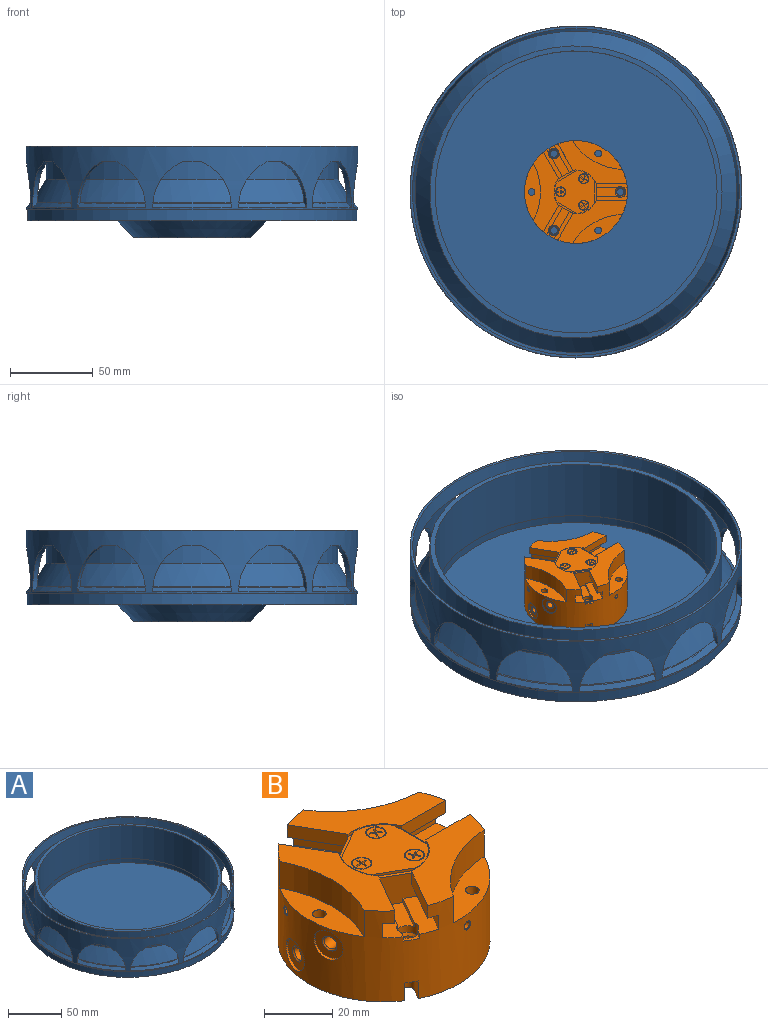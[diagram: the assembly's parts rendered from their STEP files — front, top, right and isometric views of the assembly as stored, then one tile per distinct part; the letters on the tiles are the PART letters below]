
ASSEMBLY  parts=2 mates=1
PART A: 64 faces, bbox 200x200x54.8 mm
  f0: cylinder r=100mm len=200mm, axis (0,0,1), area 11248.3mm2, adj f3,f4,f9,f10,f11,f12,f13,f14
  f1: plane 176x176mm, normal (0,0,1), area 1630.5mm2, adj f2,f5
  f2: cylinder r=85mm len=170mm, axis (0,0,1), area 20209.2mm2, adj f1,f61
  f3: plane 200x200mm, normal (0,0,-1), area 398.3mm2, adj f0,f58
  f4: plane 200x200mm, normal (0,0,1), area 935.4mm2, adj f0,f7
  f5: cylinder r=88mm len=176mm, axis (0,0,1), area 10969.9mm2, adj f1,f8
  f6: cylinder r=97mm len=194mm, axis (0,0,1), area 4810mm2, adj f7,f8,f9,f10,f11,f12,f13,f14
  f7: cone r=97mm half-angle=9.5deg, axis (0,0,1), area 5603.9mm2, adj f4,f6
  f8: cone r=88mm half-angle=31.3deg, axis (0,0,-1), area 10065.3mm2, adj f5,f6
  f9: plane 10.97x3.16mm, normal (0,0,-1), area 32.9mm2, adj f0,f6,f10,f11
  f10: cylinder r=28.77mm len=27.57mm, axis (0,-1,0), area 102.7mm2, adj f0,f6,f9,f12
  f11: cylinder r=28.77mm len=27.57mm, axis (0,-1,0), area 102.7mm2, adj f0,f6,f9,f12
  f12: cone r=100mm half-angle=45deg, axis (0,0,-1), area 202.5mm2, adj f0,f6,f10,f11
  f13: plane 11x8.09mm, normal (0,0,-1), area 32.9mm2, adj f0,f6,f14,f15
  f14: cylinder r=28.77mm len=27.57mm, axis (0.5,-0.87,0), area 102.7mm2, adj f0,f6,f13,f16
  f15: cylinder r=28.77mm len=27.57mm, axis (0.5,-0.87,0), area 102.7mm2, adj f0,f6,f13,f16
  f16: cone r=100mm half-angle=45deg, axis (0,0,-1), area 202.5mm2, adj f0,f6,f14,f15
  f17: cylinder r=28.77mm len=27.57mm, axis (0.87,-0.5,0), area 102.7mm2, adj f0,f6,f18,f20
  f18: plane 11x8.09mm, normal (0,0,-1), area 32.9mm2, adj f0,f6,f17,f19
  f19: cylinder r=28.77mm len=27.57mm, axis (0.87,-0.5,0), area 102.7mm2, adj f0,f6,f18,f20
  f20: cone r=100mm half-angle=45deg, axis (0,0,-1), area 202.5mm2, adj f0,f6,f17,f19
  f21: cylinder r=28.77mm len=27.57mm, axis (1,0,0), area 102.7mm2, adj f0,f6,f22,f24
  f22: plane 10.97x3.16mm, normal (0,0,-1), area 32.9mm2, adj f0,f6,f21,f23
  f23: cylinder r=28.77mm len=27.57mm, axis (1,0,0), area 102.7mm2, adj f0,f6,f22,f24
  f24: cone r=100mm half-angle=45deg, axis (0,0,-1), area 202.5mm2, adj f0,f6,f21,f23
  f25: cylinder r=28.77mm len=27.57mm, axis (0.87,0.5,0), area 102.7mm2, adj f0,f6,f26,f28
  f26: plane 11x8.09mm, normal (0,0,-1), area 32.9mm2, adj f0,f6,f25,f27
  f27: cylinder r=28.77mm len=27.57mm, axis (0.87,0.5,0), area 102.7mm2, adj f0,f6,f26,f28
  f28: cone r=100mm half-angle=45deg, axis (0,0,-1), area 202.5mm2, adj f0,f6,f25,f27
  f29: cylinder r=28.77mm len=27.57mm, axis (0.5,0.87,0), area 102.7mm2, adj f0,f6,f30,f32
  f30: plane 11x8.09mm, normal (0,0,-1), area 32.9mm2, adj f0,f6,f29,f31
  f31: cylinder r=28.77mm len=27.57mm, axis (0.5,0.87,0), area 102.7mm2, adj f0,f6,f30,f32
  f32: cone r=100mm half-angle=45deg, axis (0,0,-1), area 202.5mm2, adj f0,f6,f29,f31
  f33: cylinder r=28.77mm len=27.57mm, axis (0,1,0), area 102.7mm2, adj f0,f6,f34,f36
  f34: plane 10.97x3.16mm, normal (0,0,-1), area 32.9mm2, adj f0,f6,f33,f35
  f35: cylinder r=28.77mm len=27.57mm, axis (0,1,0), area 102.7mm2, adj f0,f6,f34,f36
  f36: cone r=100mm half-angle=45deg, axis (0,0,-1), area 202.5mm2, adj f0,f6,f33,f35
  f37: cylinder r=28.77mm len=27.57mm, axis (-0.5,0.87,0), area 102.7mm2, adj f0,f6,f38,f40
  f38: plane 11x8.09mm, normal (0,0,-1), area 32.9mm2, adj f0,f6,f37,f39
  f39: cylinder r=28.77mm len=27.57mm, axis (-0.5,0.87,0), area 102.7mm2, adj f0,f6,f38,f40
  f40: cone r=100mm half-angle=45deg, axis (0,0,-1), area 202.5mm2, adj f0,f6,f37,f39
  f41: plane 11x8.09mm, normal (0,0,-1), area 32.9mm2, adj f0,f6,f42,f43
  f42: cylinder r=28.77mm len=27.57mm, axis (-0.87,0.5,0), area 102.7mm2, adj f0,f6,f41,f44
  f43: cylinder r=28.77mm len=27.57mm, axis (-0.87,0.5,0), area 102.7mm2, adj f0,f6,f41,f44
  f44: cone r=100mm half-angle=45deg, axis (0,0,-1), area 202.5mm2, adj f0,f6,f42,f43
  f45: plane 10.97x3.16mm, normal (0,0,-1), area 32.9mm2, adj f0,f6,f46,f47
  f46: cylinder r=28.77mm len=27.57mm, axis (-1,0,0), area 102.7mm2, adj f0,f6,f45,f48
  f47: cylinder r=28.77mm len=27.57mm, axis (-1,0,0), area 102.7mm2, adj f0,f6,f45,f48
  f48: cone r=100mm half-angle=45deg, axis (0,0,-1), area 202.5mm2, adj f0,f6,f46,f47
  f49: plane 11x8.09mm, normal (0,0,-1), area 32.9mm2, adj f0,f6,f50,f51
  f50: cylinder r=28.77mm len=27.57mm, axis (-0.87,-0.5,0), area 102.7mm2, adj f0,f6,f49,f52
  f51: cylinder r=28.77mm len=27.57mm, axis (-0.87,-0.5,0), area 102.7mm2, adj f0,f6,f49,f52
  f52: cone r=100mm half-angle=45deg, axis (0,0,-1), area 202.5mm2, adj f0,f6,f50,f51
  f53: plane 11x8.09mm, normal (0,0,-1), area 32.9mm2, adj f0,f6,f54,f55
  f54: cylinder r=28.77mm len=27.57mm, axis (-0.5,-0.87,0), area 102.7mm2, adj f0,f6,f53,f56
  f55: cylinder r=28.77mm len=27.57mm, axis (-0.5,-0.87,0), area 102.7mm2, adj f0,f6,f53,f56
  f56: cone r=100mm half-angle=45deg, axis (0,0,-1), area 202.5mm2, adj f0,f6,f54,f55
  f57: plane 198.73x198.73mm, normal (0,0,-1), area 24655.9mm2, adj f58,f63
  f58: cylinder r=99.36mm len=198.73mm, axis (0,0,1), area 4370.3mm2, adj f3,f57
  f59: cylinder r=85.05mm len=170.1mm, axis (0,0,1), area 2671.9mm2, adj f60,f61
  f60: plane 170.1x170.1mm, normal (0,0,1), area 22725.1mm2, adj f59
  f61: plane 170.1x170.1mm, normal (0,0,-1), area 27.1mm2, adj f2,f59
  f62: plane 70x70mm, normal (0,0,-1), area 3848.5mm2, adj f63
  f63: cone r=35mm half-angle=45deg, axis (0,0,1), area 3554.3mm2, adj f57,f62
PART B: 183 faces, bbox 62.3x62x32.5 mm
  f0: plane 4.13x4.03mm, normal (-0.97,-0.22,0), area 10.9mm2, adj f1,f2,f163,f165
  f1: cylinder r=2.07mm len=5.38mm, axis (-0.97,-0.22,0), area 53.1mm2, adj f0,f2,f43,f164,f165
  f2: cylinder r=2.07mm len=0.55mm, axis (-0.97,-0.22,0), area 0mm2, adj f0,f1,f165
  f3: plane 4.13x4.03mm, normal (-0.97,0.22,0), area 11.7mm2, adj f4,f159,f161
  f4: cylinder r=2.07mm len=5.38mm, axis (-0.97,0.22,0), area 54mm2, adj f3,f40,f160,f161
  f5: cylinder r=31mm len=62mm, axis (0,0,-1), area 4600.2mm2, adj f9,f10,f11,f12,f13,f14,f18,f19
  f6: cylinder r=2.18mm len=7.57mm, axis (0,0,-1), area 68.3mm2, adj f9,f10,f81,f90,f158
  f7: cylinder r=2.18mm len=7.57mm, axis (0,0,-1), area 68.3mm2, adj f11,f12,f85,f91,f158
  f8: cylinder r=2.18mm len=7.57mm, axis (0,0,-1), area 68.3mm2, adj f13,f14,f89,f92,f158
  f9: plane 6.32x3.09mm, normal (0.87,-0.5,0), area 22.6mm2, adj f5,f6,f90,f158
  f10: plane 6.32x3.09mm, normal (-0.87,0.5,0), area 22.6mm2, adj f5,f6,f90,f158
  f11: plane 6.32x3.09mm, normal (0.87,0.5,0), area 22.6mm2, adj f5,f7,f91,f158
  f12: plane 6.32x3.09mm, normal (-0.87,-0.5,0), area 22.6mm2, adj f5,f7,f91,f158
  f13: plane 6.32x3.57mm, normal (0,-1,0), area 22.6mm2, adj f5,f8,f92,f158
  f14: plane 6.32x3.57mm, normal (0,1,0), area 22.6mm2, adj f5,f8,f92,f158
  f15: cone r=0mm half-angle=45deg, axis (0,0,1), area 6.3mm2, adj f112,f143
  f16: cone r=0mm half-angle=45deg, axis (0,0,1), area 6.3mm2, adj f112,f128
  f17: cone r=0mm half-angle=45deg, axis (0,0,1), area 6.3mm2, adj f112,f113
  f18: plane 41.56x25.92mm, normal (0,0,1), area 418mm2, adj f5,f52,f62,f75,f102
  f19: plane 47.99x15.19mm, normal (0,0,1), area 418mm2, adj f5,f53,f70,f73,f104
  f20: plane 14.77x10.14mm, normal (-0.5,0.87,0), area 129.5mm2, adj f29,f30,f31,f45,f46,f47,f49,f50
  f21: plane 17.05x10.14mm, normal (1,0,0), area 129.5mm2, adj f24,f25,f26,f54,f55,f56,f58,f59
  f22: plane 14.77x10.14mm, normal (-0.5,-0.87,0), area 129.5mm2, adj f34,f36,f63,f64,f65,f66,f67,f68
  f23: plane 2.19x1.5mm, normal (0,1,0), area 3.3mm2, adj f5,f56,f57,f86
  f24: plane 12.67x1.5mm, normal (0,1,0), area 19mm2, adj f21,f25,f56,f86
  f25: plane 12.67x5mm, normal (0,0,1), area 59.1mm2, adj f21,f24,f26,f86
  f26: plane 12.67x1.5mm, normal (0,-1,0), area 19mm2, adj f21,f25,f58,f86
  f27: plane 2.19x1.5mm, normal (0,-1,0), area 3.3mm2, adj f5,f57,f58,f86
  f28: plane 1.89x1.5mm, normal (-0.87,-0.5,0), area 3.3mm2, adj f5,f47,f48,f82
  f29: plane 10.97x6.33mm, normal (-0.87,-0.5,0), area 19mm2, adj f20,f30,f47,f82
  f30: plane 13.47x10.66mm, normal (0,0,1), area 59.1mm2, adj f20,f29,f31,f82
  f31: plane 10.97x6.33mm, normal (0.87,0.5,0), area 19mm2, adj f20,f30,f49,f82
  f32: plane 1.89x1.5mm, normal (0.87,0.5,0), area 3.3mm2, adj f5,f48,f49,f82
  f33: plane 1.89x1.5mm, normal (0.87,-0.5,0), area 3.3mm2, adj f5,f35,f65,f78
  f34: plane 10.97x6.33mm, normal (0.87,-0.5,0), area 19mm2, adj f22,f65,f66,f78
  f35: plane 5.42x4.39mm, normal (0,0,1), area 7mm2, adj f5,f33,f37,f78
  f36: plane 10.97x6.33mm, normal (-0.87,0.5,0), area 19mm2, adj f22,f66,f67,f78
  f37: plane 1.89x1.5mm, normal (-0.87,0.5,0), area 3.3mm2, adj f5,f35,f67,f78
  f38: plane 41.56x25.92mm, normal (0,0,1), area 418mm2, adj f5,f61,f71,f77,f103
  f39: cylinder r=5mm len=10mm, axis (-0.97,0.22,0), area 25.1mm2, adj f5,f41
  f40: cone r=2.07mm half-angle=45deg, axis (-0.97,0.22,0), area 8.8mm2, adj f4,f41
  f41: plane 10x9.74mm, normal (-0.97,0.22,0), area 58.9mm2, adj f39,f40
  f42: cylinder r=5mm len=10mm, axis (-0.97,-0.22,0), area 25.1mm2, adj f5,f44
  f43: cone r=2.07mm half-angle=45deg, axis (-0.97,-0.22,0), area 8.8mm2, adj f1,f44
  f44: plane 10x9.74mm, normal (-0.97,-0.22,0), area 58.9mm2, adj f42,f43
  f45: plane 17.09x12.3mm, normal (0,0,-1), area 63.9mm2, adj f5,f20,f46,f52
  f46: plane 15.33x8.85mm, normal (-0.87,-0.5,0), area 89.4mm2, adj f5,f20,f45,f47
  f47: plane 18.34x14.62mm, normal (0,0,1), area 108.7mm2, adj f5,f20,f28,f29,f46,f82
  f48: plane 5.42x4.39mm, normal (0,0,1), area 7mm2, adj f5,f28,f32,f82
  f49: plane 19.29x14.07mm, normal (0,0,1), area 108.7mm2, adj f5,f20,f31,f32,f50,f82
  f50: plane 15.33x8.85mm, normal (0.87,0.5,0), area 89.4mm2, adj f5,f20,f49,f51
  f51: plane 17.78x11.9mm, normal (0,0,-1), area 63.9mm2, adj f5,f20,f50,f53
  f52: plane 16.01x9.25mm, normal (-0.87,-0.5,0), area 83.1mm2, adj f5,f18,f20,f45,f102,f105
  f53: plane 16.01x9.25mm, normal (0.87,0.5,0), area 83.1mm2, adj f5,f19,f20,f51,f104,f105
  f54: plane 18.49x3.53mm, normal (0,0,-1), area 63.9mm2, adj f5,f21,f55,f61
  f55: plane 17.7x5.05mm, normal (0,1,0), area 89.4mm2, adj f5,f21,f54,f56
  f56: plane 18.8x6.03mm, normal (0,0,1), area 108.7mm2, adj f5,f21,f23,f24,f55,f86
  f57: plane 5x2.29mm, normal (0,0,1), area 7mm2, adj f5,f23,f27,f86
  f58: plane 18.8x6.03mm, normal (0,0,1), area 108.7mm2, adj f5,f21,f26,f27,f59,f86
  f59: plane 17.7x5.05mm, normal (0,-1,0), area 89.4mm2, adj f5,f21,f58,f60
  f60: plane 18.49x3.53mm, normal (0,0,-1), area 63.9mm2, adj f5,f21,f59,f62
  f61: plane 18.49x4.5mm, normal (0,1,0), area 83.1mm2, adj f5,f21,f38,f54,f103,f105
  f62: plane 18.49x4.5mm, normal (0,-1,0), area 83.1mm2, adj f5,f18,f21,f60,f102,f105
  f63: plane 17.78x11.9mm, normal (0,0,-1), area 63.9mm2, adj f5,f22,f64,f70
  f64: plane 15.33x8.85mm, normal (0.87,-0.5,0), area 89.4mm2, adj f5,f22,f63,f65
  f65: plane 19.29x14.07mm, normal (0,0,1), area 108.7mm2, adj f5,f22,f33,f34,f64,f78
  f66: plane 13.47x10.66mm, normal (0,0,1), area 59.1mm2, adj f22,f34,f36,f78
  f67: plane 18.34x14.62mm, normal (0,0,1), area 108.7mm2, adj f5,f22,f36,f37,f68,f78
  f68: plane 15.33x8.85mm, normal (-0.87,0.5,0), area 89.4mm2, adj f5,f22,f67,f69
  f69: plane 17.09x12.3mm, normal (0,0,-1), area 63.9mm2, adj f5,f22,f68,f71
  f70: plane 16.01x9.25mm, normal (0.87,-0.5,0), area 83.1mm2, adj f5,f19,f22,f63,f104,f105
  f71: plane 16.01x9.25mm, normal (-0.87,0.5,0), area 83.1mm2, adj f5,f22,f38,f69,f103,f105
  f72: plane 34.8x9.56mm, normal (0,0,1), area 212.7mm2, adj f5,f73,f180
  f73: cylinder r=38mm len=34.8mm, axis (0,0,-1), area 343.4mm2, adj f5,f19,f72
  f74: plane 30.14x17.48mm, normal (0,0,1), area 212.7mm2, adj f5,f75,f170
  f75: cylinder r=38mm len=30.14mm, axis (0,0,-1), area 343.4mm2, adj f5,f18,f74
  f76: plane 30.14x17.48mm, normal (0,0,1), area 212.7mm2, adj f5,f77,f174
  f77: cylinder r=38mm len=30.14mm, axis (0,0,-1), area 343.4mm2, adj f5,f38,f76
  f78: cylinder r=3.18mm len=6.37mm, axis (0,0,-1), area 61.5mm2, adj f33,f34,f35,f36,f37,f65,f66,f67
  f79: cone r=3.18mm half-angle=30deg, axis (0,0,1), area 19.4mm2, adj f78,f80
  f80: cylinder r=2.65mm len=10.26mm, axis (0,0,-1), area 171.1mm2, adj f79,f81
  f81: cone r=2.65mm half-angle=60deg, axis (0,0,1), area 8.2mm2, adj f6,f80
  f82: cylinder r=3.18mm len=6.37mm, axis (0,0,-1), area 61.5mm2, adj f28,f29,f30,f31,f32,f47,f48,f49
  f83: cone r=3.18mm half-angle=30deg, axis (0,0,1), area 19.4mm2, adj f82,f84
  f84: cylinder r=2.65mm len=10.26mm, axis (0,0,-1), area 171.1mm2, adj f83,f85
  f85: cone r=2.65mm half-angle=60deg, axis (0,0,1), area 8.2mm2, adj f7,f84
  f86: cylinder r=3.18mm len=6.37mm, axis (0,0,-1), area 61.5mm2, adj f23,f24,f25,f26,f27,f56,f57,f58
  f87: cone r=3.18mm half-angle=30deg, axis (0,0,1), area 19.4mm2, adj f86,f88
  f88: cylinder r=2.65mm len=10.26mm, axis (0,0,-1), area 171.1mm2, adj f87,f89
  f89: cone r=2.65mm half-angle=60deg, axis (0,0,1), area 8.2mm2, adj f8,f88
  f90: plane 5.42x5.19mm, normal (0,0,-1), area 10.3mm2, adj f5,f6,f9,f10
  f91: plane 5.42x5.19mm, normal (0,0,-1), area 10.3mm2, adj f5,f7,f11,f12
  f92: plane 4.19x3.64mm, normal (0,0,-1), area 10.3mm2, adj f5,f8,f13,f14
  f93: cone r=1.5mm half-angle=45deg, axis (-0.92,0.39,0), area 2.8mm2, adj f5,f94
  f94: cylinder r=1.23mm len=9.29mm, axis (0.92,-0.39,0), area 69.9mm2, adj f93,f95
  f95: plane 2.46x2.26mm, normal (-0.92,0.39,0), area 4.7mm2, adj f94
  f96: cone r=1.5mm half-angle=45deg, axis (0.12,-0.99,0), area 2.8mm2, adj f5,f97
  f97: cylinder r=1.23mm len=9.28mm, axis (-0.12,0.99,0), area 69.9mm2, adj f96,f98
  f98: plane 2.46x2.44mm, normal (0.12,-0.99,0), area 4.7mm2, adj f97
  f99: cone r=1.5mm half-angle=45deg, axis (0.8,0.6,0), area 2.7mm2, adj f5,f100
  f100: cylinder r=1.23mm len=8.71mm, axis (-0.8,-0.6,0), area 69.9mm2, adj f99,f101
  f101: plane 2.46x1.96mm, normal (0.8,0.6,0), area 4.7mm2, adj f100
  f102: cylinder r=13.25mm len=14.07mm, axis (0,0,1), area 16mm2, adj f18,f52,f62,f105
  f103: cylinder r=13.25mm len=14.07mm, axis (0,0,1), area 16mm2, adj f38,f61,f71,f105
  f104: cylinder r=13.25mm len=16.25mm, axis (0,0,1), area 16mm2, adj f19,f53,f70,f105
  f105: plane 26.49x25.51mm, normal (0,0,1), area 52.8mm2, adj f20,f21,f22,f52,f53,f61,f62,f70
  f106: plane 11.94x6.89mm, normal (-0.5,0.87,0), area 11.2mm2, adj f105,f107,f111,f112
  f107: cylinder r=12.98mm len=12.16mm, axis (0,0,-1), area 10.3mm2, adj f105,f106,f108,f112
  f108: plane 11.94x6.89mm, normal (-0.5,-0.87,0), area 11.2mm2, adj f105,f107,f109,f112
  f109: cylinder r=12.98mm len=10.53mm, axis (0,0,-1), area 10.3mm2, adj f105,f108,f110,f112
  f110: plane 13.78x0.81mm, normal (1,0,0), area 11.2mm2, adj f105,f109,f111,f112
  f111: cylinder r=12.98mm len=10.53mm, axis (0,0,-1), area 10.3mm2, adj f105,f106,f110,f112
  f112: plane 25.94x23.98mm, normal (0,0,1), area 389.1mm2, adj f15,f16,f17,f106,f107,f108,f109,f110
  f113: cylinder r=2.75mm len=5.5mm, axis (0,0,1), area 4mm2, adj f17,f114
  f114: plane 5.5x5.5mm, normal (0,0,1), area 20mm2, adj f113,f115,f116,f117,f118,f119,f120,f121
  f115: plane 1x0.54mm, normal (1,0,0), area 0.5mm2, adj f114,f116,f126,f127
  f116: plane 1.59x1mm, normal (0,1,0), area 1.6mm2, adj f114,f115,f117,f127
  f117: plane 1.59x1mm, normal (1,0,0), area 1.6mm2, adj f114,f116,f118,f127
  f118: plane 1x0.54mm, normal (0,1,0), area 0.5mm2, adj f114,f117,f119,f127
  f119: plane 1.59x1mm, normal (-1,0,0), area 1.6mm2, adj f114,f118,f120,f127
  f120: plane 1.59x1mm, normal (0,1,0), area 1.6mm2, adj f114,f119,f121,f127
  f121: plane 1x0.54mm, normal (-1,0,0), area 0.5mm2, adj f114,f120,f122,f127
  f122: plane 1.59x1mm, normal (0,-1,0), area 1.6mm2, adj f114,f121,f123,f127
  f123: plane 1.59x1mm, normal (-1,0,0), area 1.6mm2, adj f114,f122,f124,f127
  f124: plane 1x0.54mm, normal (0,-1,0), area 0.5mm2, adj f114,f123,f125,f127
  f125: plane 1.59x1mm, normal (1,0,0), area 1.6mm2, adj f114,f124,f126,f127
  f126: plane 1.59x1mm, normal (0,-1,0), area 1.6mm2, adj f114,f115,f125,f127
  f127: plane 3.72x3.72mm, normal (0,0,1), area 3.7mm2, adj f115,f116,f117,f118,f119,f120,f121,f122
  f128: cylinder r=2.75mm len=5.5mm, axis (0,0,1), area 4mm2, adj f16,f129
  f129: plane 5.5x5.5mm, normal (0,0,1), area 20mm2, adj f128,f130,f131,f132,f133,f134,f135,f136
  f130: plane 1x0.47mm, normal (-0.5,-0.87,0), area 0.5mm2, adj f129,f131,f141,f142
  f131: plane 1.38x1mm, normal (0.87,-0.5,0), area 1.6mm2, adj f129,f130,f132,f142
  f132: plane 1.38x1mm, normal (-0.5,-0.87,0), area 1.6mm2, adj f129,f131,f133,f142
  f133: plane 1x0.47mm, normal (0.87,-0.5,0), area 0.5mm2, adj f129,f132,f134,f142
  f134: plane 1.38x1mm, normal (0.5,0.87,0), area 1.6mm2, adj f129,f133,f135,f142
  f135: plane 1.38x1mm, normal (0.87,-0.5,0), area 1.6mm2, adj f129,f134,f136,f142
  f136: plane 1x0.47mm, normal (0.5,0.87,0), area 0.5mm2, adj f129,f135,f137,f142
  f137: plane 1.38x1mm, normal (-0.87,0.5,0), area 1.6mm2, adj f129,f136,f138,f142
  f138: plane 1.38x1mm, normal (0.5,0.87,0), area 1.6mm2, adj f129,f137,f139,f142
  f139: plane 1x0.47mm, normal (-0.87,0.5,0), area 0.5mm2, adj f129,f138,f140,f142
  f140: plane 1.38x1mm, normal (-0.5,-0.87,0), area 1.6mm2, adj f129,f139,f141,f142
  f141: plane 1.38x1mm, normal (-0.87,0.5,0), area 1.6mm2, adj f129,f130,f140,f142
  f142: plane 3.49x3.49mm, normal (0,0,1), area 3.7mm2, adj f130,f131,f132,f133,f134,f135,f136,f137
  f143: cylinder r=2.75mm len=5.5mm, axis (0,0,1), area 4mm2, adj f15,f144
  f144: plane 5.5x5.5mm, normal (0,0,1), area 20mm2, adj f143,f145,f146,f147,f148,f149,f150,f151
  f145: plane 1x0.47mm, normal (-0.5,0.87,0), area 0.5mm2, adj f144,f146,f156,f157
  f146: plane 1.38x1mm, normal (-0.87,-0.5,0), area 1.6mm2, adj f144,f145,f147,f157
  f147: plane 1.38x1mm, normal (-0.5,0.87,0), area 1.6mm2, adj f144,f146,f148,f157
  f148: plane 1x0.47mm, normal (-0.87,-0.5,0), area 0.5mm2, adj f144,f147,f149,f157
  f149: plane 1.38x1mm, normal (0.5,-0.87,0), area 1.6mm2, adj f144,f148,f150,f157
  f150: plane 1.38x1mm, normal (-0.87,-0.5,0), area 1.6mm2, adj f144,f149,f151,f157
  f151: plane 1x0.47mm, normal (0.5,-0.87,0), area 0.5mm2, adj f144,f150,f152,f157
  f152: plane 1.38x1mm, normal (0.87,0.5,0), area 1.6mm2, adj f144,f151,f153,f157
  f153: plane 1.38x1mm, normal (0.5,-0.87,0), area 1.6mm2, adj f144,f152,f154,f157
  f154: plane 1x0.47mm, normal (0.87,0.5,0), area 0.5mm2, adj f144,f153,f155,f157
  f155: plane 1.38x1mm, normal (-0.5,0.87,0), area 1.6mm2, adj f144,f154,f156,f157
  f156: plane 1.38x1mm, normal (0.87,0.5,0), area 1.6mm2, adj f144,f145,f155,f157
  f157: plane 3.49x3.49mm, normal (0,0,1), area 3.7mm2, adj f145,f146,f147,f148,f149,f150,f151,f152
  f158: plane 62x61.93mm, normal (0,0,-1), area 2846.6mm2, adj f5,f6,f7,f8,f9,f10,f11,f12
  f159: plane 1.55x0.49mm, normal (0,0,-1), area 0.3mm2, adj f3,f161
  f160: plane 1.8x0.65mm, normal (0,0,-1), area 0.5mm2, adj f4,f161
  f161: cylinder r=1.23mm len=5.73mm, axis (0,0,-1), area 39.1mm2, adj f3,f4,f159,f160,f162
  f162: cone r=1.23mm half-angle=45deg, axis (0,0,-1), area 2.9mm2, adj f158,f161
  f163: plane 1.55x0.49mm, normal (0,0,-1), area 0.3mm2, adj f0,f165
  f164: plane 1.69x0.58mm, normal (0,0,-1), area 0.4mm2, adj f1,f165
  f165: cylinder r=1.23mm len=16.73mm, axis (0,0,-1), area 122.1mm2, adj f0,f1,f2,f163,f164,f166
  f166: cone r=1.23mm half-angle=45deg, axis (0,0,-1), area 2.9mm2, adj f158,f165
  f167: cone r=2.5mm half-angle=45deg, axis (0,0,-1), area 8.2mm2, adj f158,f168
  f168: cylinder r=2.07mm len=9.07mm, axis (0,0,1), area 117.8mm2, adj f167,f169
  f169: plane 4.13x4.13mm, normal (0,0,-1), area 0.9mm2, adj f168,f170
  f170: cylinder r=2mm len=13.53mm, axis (0,0,1), area 170mm2, adj f74,f169
  f171: cone r=2.5mm half-angle=45deg, axis (0,0,-1), area 8.2mm2, adj f158,f172
  f172: cylinder r=2.07mm len=9.07mm, axis (0,0,1), area 117.8mm2, adj f171,f173
  f173: plane 4.13x4.13mm, normal (0,0,-1), area 0.9mm2, adj f172,f174
  f174: cylinder r=2mm len=13.53mm, axis (0,0,1), area 170mm2, adj f76,f173
  f175: cylinder r=2mm len=7.97mm, axis (0,0,-1), area 100.2mm2, adj f158,f176
  f176: plane 4x4mm, normal (0,0,-1), area 12.6mm2, adj f175
  f177: cone r=2.5mm half-angle=45deg, axis (0,0,-1), area 8.2mm2, adj f158,f178
  f178: cylinder r=2.07mm len=9.07mm, axis (0,0,1), area 117.8mm2, adj f177,f179
  f179: plane 4.13x4.13mm, normal (0,0,-1), area 0.9mm2, adj f178,f180
  f180: cylinder r=2mm len=13.53mm, axis (0,0,1), area 170mm2, adj f72,f179
  f181: cylinder r=2mm len=7.97mm, axis (0,0,-1), area 100.2mm2, adj f158,f182
  f182: plane 4x4mm, normal (0,0,-1), area 12.6mm2, adj f181
PLACE A t=(-120.68,-68.18,260.97)mm
PLACE B t=(-120.68,-68.18,218.1)mm
MATE fastened B.f5 <-> A.f0  axis (0,0,-1) through (-120.68,-68.18,218.13)mm
